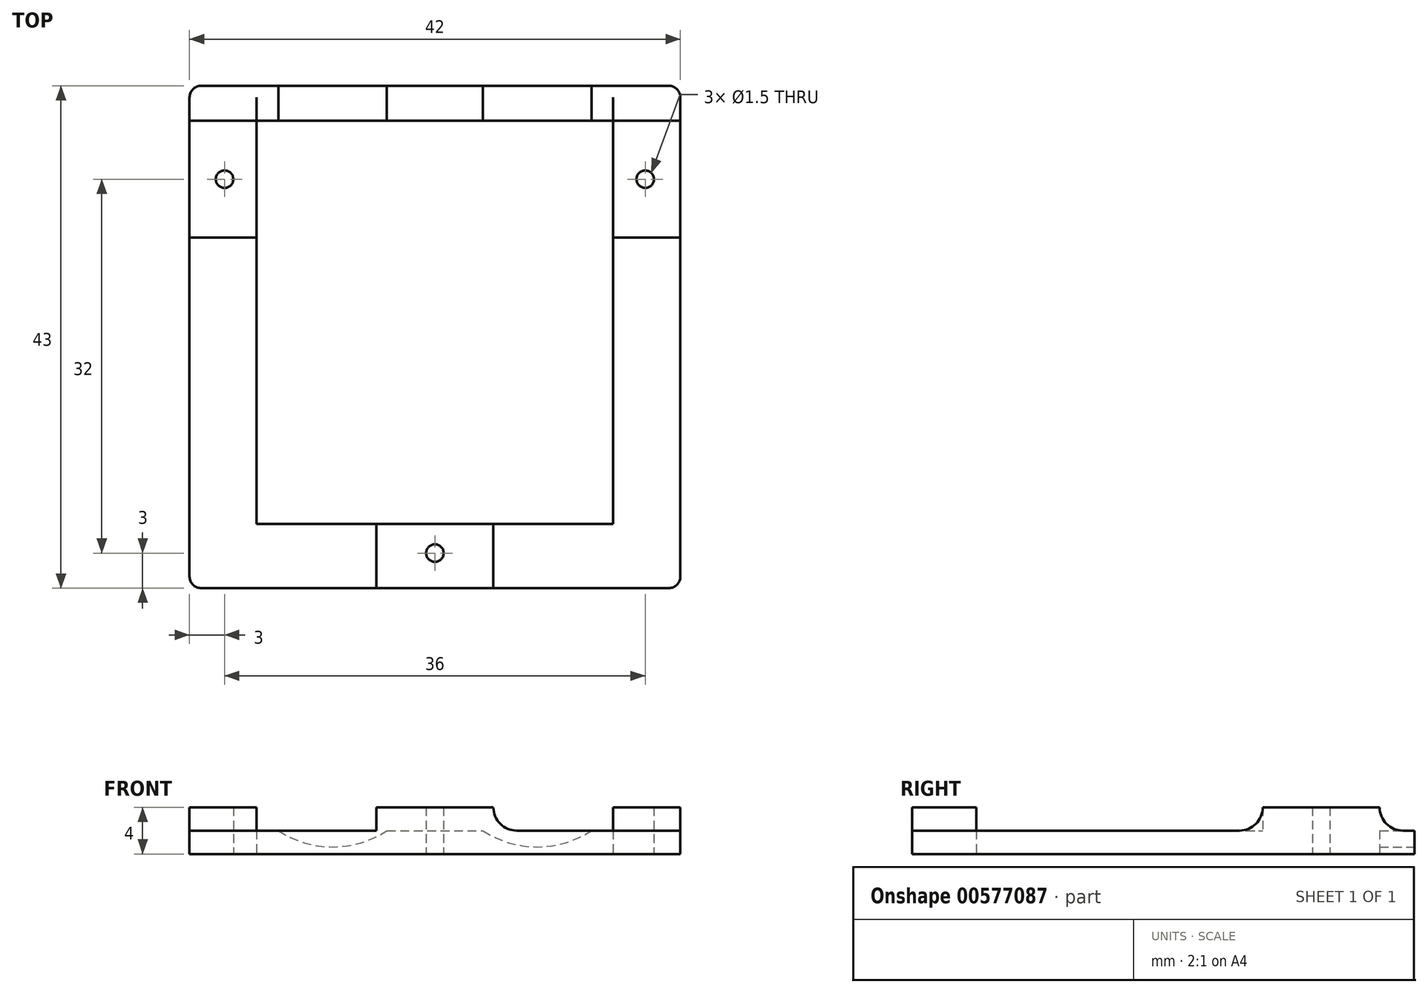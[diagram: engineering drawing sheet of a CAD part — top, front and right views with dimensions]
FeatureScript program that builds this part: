
annotation { "Feature Type Name" : "Feature", "Feature Type Description" : "" }
export const myFeature = defineFeature(function(context is Context, id is Id, definition is map)
    precondition{}
    {
        {
            var Q0;
            Q0=qCreatedBy(makeId("Top.planeOp"),FACE);
            var sketch = newSketch(context, id + "F0", { "sketchPlane" : qUnion([Q0])});
            skLineSegment(sketch, "E0", {"start": v(-15.25, 0) * mm, "end": v(15.25, 0) * mm});
            skLineSegment(sketch, "E1", {"start": v(15.25, 0) * mm, "end": v(15.25, -34.5) * mm});
            skLineSegment(sketch, "E2", {"start": v(15.25, -34.5) * mm, "end": v(-15.25, -34.5) * mm});
            skLineSegment(sketch, "E3", {"start": v(-15.25, -34.5) * mm, "end": v(-15.25, 0) * mm});
            skLineSegment(sketch, "E4", {"start": v(-21, 3) * mm, "end": v(21, 3) * mm});
            skLineSegment(sketch, "E5", {"start": v(21, 3) * mm, "end": v(21, -40) * mm});
            skLineSegment(sketch, "E6", {"start": v(21, -40) * mm, "end": v(-21, -40) * mm});
            skLineSegment(sketch, "E7", {"start": v(-21, -40) * mm, "end": v(-21, 3) * mm});
            skCircle(sketch, "E8", {"center": v(0, -37) * mm, "radius": 0.75 * mm});
            skCircle(sketch, "E9", {"center": v(18, -5) * mm, "radius": 0.75 * mm});
            skCircle(sketch, "E10", {"center": v(-18, -5) * mm, "radius": 0.75 * mm});
            skLineSegment(sketch, "E11", {"start": v(-21, -5) * mm, "end": v(21, -5) * mm, "construction": true});
            skSolve(sketch);
        }
        {
            var Q0;
            Q0=makeQuery(id+"F0.imprint","IMPRINT",FACE,{"disambiguationData":[TD([[makeQuery(id+"F0.imprint","IMPRINT",EDGE,{"derivedFrom":sQuery(id+"F0.wireOp",EDGE,"E0")}),1.0]])]});
            extrude(context, id + "F1", {"entities" : qUnion([Q0]), "depth" : 2 * mm, "offsetDistance" : 25 * mm});
        }
        {
            var Q0;
            Q0=makeQuery(id+"F1.opExtrude","CAP_FACE",FACE,{"disambiguationData":[OSD([sQuery(id+"F0.wireOp",EDGE,"E0"),sQuery(id+"F0.wireOp",EDGE,"E1"),sQuery(id+"F0.wireOp",EDGE,"E2"),sQuery(id+"F0.wireOp",EDGE,"E3"),sQuery(id+"F0.wireOp",EDGE,"E4"),sQuery(id+"F0.wireOp",EDGE,"E5"),sQuery(id+"F0.wireOp",EDGE,"E6"),sQuery(id+"F0.wireOp",EDGE,"E7"),sQuery(id+"F0.wireOp",EDGE,"E8"),sQuery(id+"F0.wireOp",EDGE,"E9"),sQuery(id+"F0.wireOp",EDGE,"E10")])],"isStart":false});
            var sketch = newSketch(context, id + "F2", { "sketchPlane" : qUnion([Q0])});
            skLineSegment(sketch, "E12", {"start": v(-15.25, 0) * mm, "end": v(-21, 0) * mm});
            skLineSegment(sketch, "E13", {"start": v(-21, 0) * mm, "end": v(-21, -10) * mm});
            skLineSegment(sketch, "E14", {"start": v(-21, -10) * mm, "end": v(-15.25, -10) * mm});
            skLineSegment(sketch, "E15", {"start": v(-15.25, -10) * mm, "end": v(-15.25, 0) * mm});
            skLineSegment(sketch, "E16", {"start": v(15.25, 0) * mm, "end": v(21, 0) * mm});
            skLineSegment(sketch, "E17", {"start": v(21, 0) * mm, "end": v(21, -10) * mm});
            skLineSegment(sketch, "E18", {"start": v(21, -10) * mm, "end": v(15.25, -10) * mm});
            skLineSegment(sketch, "E19", {"start": v(15.25, -10) * mm, "end": v(15.25, 0) * mm});
            skLineSegment(sketch, "E20", {"start": v(-5, -34.5) * mm, "end": v(-5, -40) * mm});
            skLineSegment(sketch, "E21", {"start": v(-5, -40) * mm, "end": v(5, -40) * mm});
            skLineSegment(sketch, "E22", {"start": v(5, -40) * mm, "end": v(5, -34.5) * mm});
            skLineSegment(sketch, "E23", {"start": v(5, -34.5) * mm, "end": v(-5, -34.5) * mm});
            skCircle(sketch, "E24.0", {"center": v(0, -37) * mm, "radius": 0.75 * mm});
            skCircle(sketch, "E24.1", {"center": v(-18, -5) * mm, "radius": 0.75 * mm});
            skCircle(sketch, "E24.2", {"center": v(18, -5) * mm, "radius": 0.75 * mm});
            skSolve(sketch);
        }
        {
            var Q0;
            Q0 = qSketchRegion(id + "F2", true);
            extrude(context, id + "F3", {"entities" : qUnion([Q0]), "operationType" : NewBodyOperationType.ADD, "depth" : 2 * mm, "offsetDistance" : 25 * mm});
        }
        {
            var Q0;
            Q0=makeQuery(id+"F1.opExtrude","SWEPT_FACE",FACE,{"disambiguationData":[OSD([sQuery(id+"F0.wireOp",EDGE,"E4")])]});
            var sketch = newSketch(context, id + "F4", { "sketchPlane" : qUnion([Q0])});
            skCircle(sketch, "E25", {"center": v(-8.75, 9) * mm, "radius": 8.4 * mm});
            skCircle(sketch, "E26", {"center": v(8.75, 9) * mm, "radius": 8.4 * mm});
            skSolve(sketch);
        }
        {
            var Q0;
            Q0 = qSketchRegion(id + "F4", true);
            var Q1;
            Q1=makeQuery(id+"F1.opExtrude","SWEPT_FACE",FACE,{"disambiguationData":[OSD([sQuery(id+"F0.wireOp",EDGE,"E0")])]});
            extrude(context, id + "F5", {"entities" : qUnion([Q0]), "operationType" : NewBodyOperationType.REMOVE, "endBound" : BoundingType.UP_TO_SURFACE, "oppositeDirection" : true, "depth" : 3.9 * mm, "endBoundEntityFace" : qUnion([Q1]), "offsetDistance" : 25 * mm});
        }
        {
            var Q0;
            Q0=makeQuery(id+"F3.opExtrude","CAP_EDGE",EDGE,{"disambiguationData":[OSD([sQuery(id+"F2.wireOp",EDGE,"E22")])],"isStart":true});
            var Q1;
            Q1=makeQuery(id+"F3.opExtrude","CAP_EDGE",EDGE,{"disambiguationData":[OSD([sQuery(id+"F2.wireOp",EDGE,"E18")])],"isStart":true});
            var Q2;
            Q2=makeQuery(id+"F3.opExtrude","CAP_EDGE",EDGE,{"disambiguationData":[OSD([sQuery(id+"F2.wireOp",EDGE,"E14")])],"isStart":true});
            var Q3;
            Q3=makeQuery(id+"F3.opExtrude","CAP_EDGE",EDGE,{"disambiguationData":[OSD([sQuery(id+"F2.wireOp",EDGE,"E20")])],"isStart":true});
            var Q4;
            Q4=makeQuery(id+"F3.opExtrude","CAP_EDGE",EDGE,{"disambiguationData":[OSD([sQuery(id+"F2.wireOp",EDGE,"E16")])],"isStart":true});
            var Q5;
            Q5=makeQuery(id+"F3.opExtrude","CAP_EDGE",EDGE,{"disambiguationData":[OSD([sQuery(id+"F2.wireOp",EDGE,"E12")])],"isStart":true});
            fillet(context, id + "F6", {"entities" : qUnion([Q0, Q1, Q2, Q3, Q4, Q5]), "radius" : 2 * mm, "tangentPropagation" : true, "allowEdgeOverflow" : false});
        }
        {
            var Q0;
            Q0=makeQuery(id+"F1.opExtrude","SWEPT_EDGE",EDGE,{"disambiguationData":[OSD([sQuery(id+"F0.wireOp",EDGE,"E6"),sQuery(id+"F0.wireOp",EDGE,"E7")])]});
            var Q1;
            Q1=makeQuery(id+"F1.opExtrude","SWEPT_EDGE",EDGE,{"disambiguationData":[OSD([sQuery(id+"F0.wireOp",EDGE,"E4"),sQuery(id+"F0.wireOp",EDGE,"E7")])]});
            var Q2;
            Q2=makeQuery(id+"F1.opExtrude","SWEPT_EDGE",EDGE,{"disambiguationData":[OSD([sQuery(id+"F0.wireOp",EDGE,"E5"),sQuery(id+"F0.wireOp",EDGE,"E6")])]});
            var Q3;
            Q3=makeQuery(id+"F1.opExtrude","SWEPT_EDGE",EDGE,{"disambiguationData":[OSD([sQuery(id+"F0.wireOp",EDGE,"E4"),sQuery(id+"F0.wireOp",EDGE,"E5")])]});
            fillet(context, id + "F7", {"entities" : qUnion([Q0, Q1, Q2, Q3]), "radius" : 1 * mm, "tangentPropagation" : true, "allowEdgeOverflow" : false});
        }
    });
